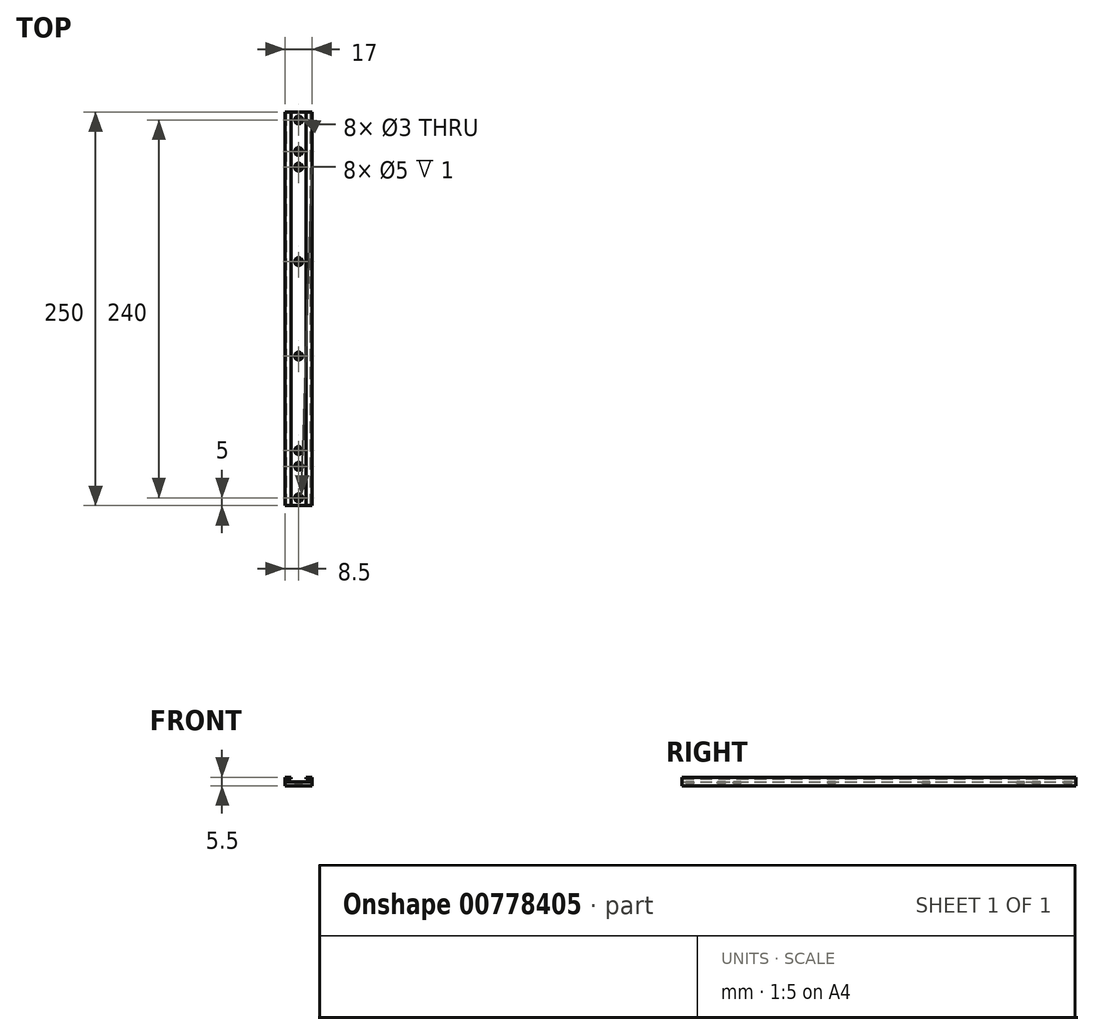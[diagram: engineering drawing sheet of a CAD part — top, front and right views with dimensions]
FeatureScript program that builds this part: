
annotation { "Feature Type Name" : "Feature", "Feature Type Description" : "" }
export const myFeature = defineFeature(function(context is Context, id is Id, definition is map)
    precondition{}
    {
        {
            var Q0;
            Q0=qCreatedBy(makeId("Front.planeOp"),FACE);
            var sketch = newSketch(context, id + "F0", { "sketchPlane" : qUnion([Q0])});
            skLineSegment(sketch, "E0.bottom", {"start": v(-8.5, 0) * mm, "end": v(8.5, 0) * mm});
            skLineSegment(sketch, "E0.top", {"start": v(-8.5, 5.5) * mm, "end": v(8.5, 5.5) * mm});
            skLineSegment(sketch, "E0.left", {"start": v(-8.5, 0) * mm, "end": v(-8.5, 5.5) * mm});
            skLineSegment(sketch, "E0.right", {"start": v(8.5, 0) * mm, "end": v(8.5, 5.5) * mm});
            skPoint(sketch, "E1", {"position": v(0, 5.5) * mm});
            skPoint(sketch, "E2", {"position": v(4.8, 5.5) * mm});
            skPoint(sketch, "E3", {"position": v(-4.8, 5.5) * mm});
            skLineSegment(sketch, "E4.bottom", {"start": v(-7.5, 4.5) * mm, "end": v(7.5, 4.5) * mm});
            skLineSegment(sketch, "E4.top", {"start": v(-7.5, 2.5) * mm, "end": v(7.5, 2.5) * mm});
            skLineSegment(sketch, "E4.left", {"start": v(-7.5, 4.5) * mm, "end": v(-7.5, 2.5) * mm});
            skLineSegment(sketch, "E4.right", {"start": v(7.5, 4.5) * mm, "end": v(7.5, 2.5) * mm});
            skLineSegment(sketch, "E5", {"start": v(4.8, 5.5) * mm, "end": v(4.8, 4.5) * mm});
            skLineSegment(sketch, "E6", {"start": v(4.8, 4.5) * mm, "end": v(4.8, 4.5) * mm});
            skLineSegment(sketch, "E7", {"start": v(-4.8, 5.5) * mm, "end": v(-4.8, 4.5) * mm});
            skSolve(sketch);
        }
        {
            var Q0;
            Q0=makeQuery(id+"F0.imprint","IMPRINT",FACE,{"disambiguationData":[TD([[makeQuery(id+"F0.imprint","IMPRINT",EDGE,{"derivedFrom":sQuery(id+"F0.wireOp",EDGE,"E0.bottom")}),1.0]])]});
            extrude(context, id + "F1", {"entities" : qUnion([Q0]), "depth" : 125 * mm, "offsetDistance" : 25 * mm, "hasSecondDirection" : true, "secondDirectionOppositeDirection" : true, "secondDirectionDepth" : 125 * mm});
        }
        {
            var Q0;
            Q0=makeQuery(id+"F1.opExtrude","SWEPT_FACE",FACE,{"disambiguationData":[OSD([sQuery(id+"F0.wireOp",EDGE,"E4.top")])]});
            var sketch = newSketch(context, id + "F2", { "sketchPlane" : qUnion([Q0])});
            skLineSegment(sketch, "E8", {"start": v(0, 0) * mm, "end": v(0, 30) * mm, "construction": true});
            skLineSegment(sketch, "E9", {"start": v(0, 0) * mm, "end": v(0, -30) * mm, "construction": true});
            skLineSegment(sketch, "E10", {"start": v(0, 30) * mm, "end": v(0, 90) * mm, "construction": true});
            skLineSegment(sketch, "E11", {"start": v(0, -30) * mm, "end": v(0, -90) * mm, "construction": true});
            skPoint(sketch, "E12", {"position": v(0, 100) * mm});
            skPoint(sketch, "E13", {"position": v(0, 120) * mm});
            skPoint(sketch, "E14", {"position": v(0, -100) * mm});
            skPoint(sketch, "E15", {"position": v(0, -120) * mm});
            skSolve(sketch);
        }
        {
            var Q0;
            Q0=sQuery(id+"F2.wireOp",VERTEX,"E11.end");
            var Q1;
            Q1=sQuery(id+"F2.wireOp",VERTEX,"E9.end");
            var Q2;
            Q2=sQuery(id+"F2.wireOp",VERTEX,"E8.end");
            var Q3;
            Q3=sQuery(id+"F2.wireOp",VERTEX,"E10.end");
            var Q4;
            Q4=sQuery(id+"F2.wireOp",VERTEX,"E13");
            var Q5;
            Q5=sQuery(id+"F2.wireOp",VERTEX,"E12");
            var Q6;
            Q6=sQuery(id+"F2.wireOp",VERTEX,"E15");
            var Q7;
            Q7=sQuery(id+"F2.wireOp",VERTEX,"E14");
            var Q8;
            Q8=makeQuery(id+"F1.opExtrude","SWEPT_BODY",BODY,{"disambiguationData":[OSD([sQuery(id+"F0.wireOp",EDGE,"E0.bottom"),sQuery(id+"F0.wireOp",EDGE,"E0.top"),sQuery(id+"F0.wireOp",EDGE,"E0.left"),sQuery(id+"F0.wireOp",EDGE,"E0.right"),sQuery(id+"F0.wireOp",EDGE,"E4.bottom"),sQuery(id+"F0.wireOp",EDGE,"E4.top"),sQuery(id+"F0.wireOp",EDGE,"E4.left"),sQuery(id+"F0.wireOp",EDGE,"E4.right"),sQuery(id+"F0.wireOp",EDGE,"E5"),sQuery(id+"F0.wireOp",EDGE,"E7")])]});
            hole(context, id + "F3", {"style" : HoleStyle.C_BORE, "endStyle" : HoleEndStyle.THROUGH, "holeDiameter" : 3 * mm, "cBoreDiameter" : 5 * mm, "cBoreDepth" : 1 * mm, "majorDiameter" : 5 * mm, "isTappedThrough" : true, "tappedDepth" : 12 * mm, "tapClearance" : 3, "locations" : qUnion([Q0, Q1, Q2, Q3, Q4, Q5, Q6, Q7]), "scope" : qUnion([Q8])});
        }
    });
